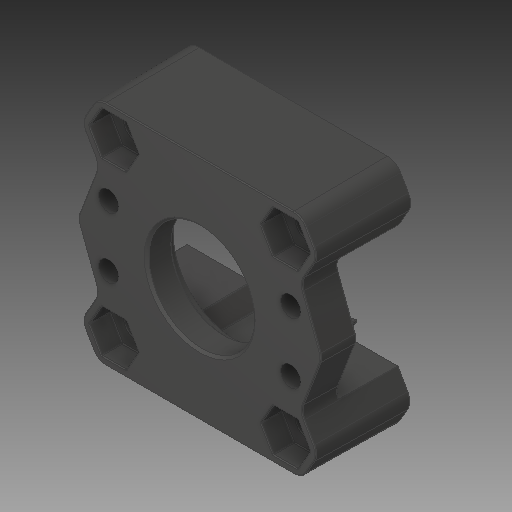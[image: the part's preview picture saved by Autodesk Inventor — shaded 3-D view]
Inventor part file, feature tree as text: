
AUTODESK INVENTOR PART (.ipt)
format: ipt  version: 2018 (Build 220112000, 112)  size: 2,122,240 bytes
history: native  units: in
note: dims shown in document units (in); Inventor stores cm internally (conversion verified against a paired STEP export)
features: chamfer x1
ambient origin geometry x8: Origin, YZ Plane, XZ Plane, XY Plane, X Axis, Y Axis, Z Axis, Center Point
bodies: Solid1 (feature_tree)
feature tree (1):
  chamfer  "Chamfer1"  [1 undecoded]
note: 1 required parameter value undecoded (feature->parameter linkage not recoverable at this tier; creation-order binding heuristic only, values carry confidence <= 0.55)
